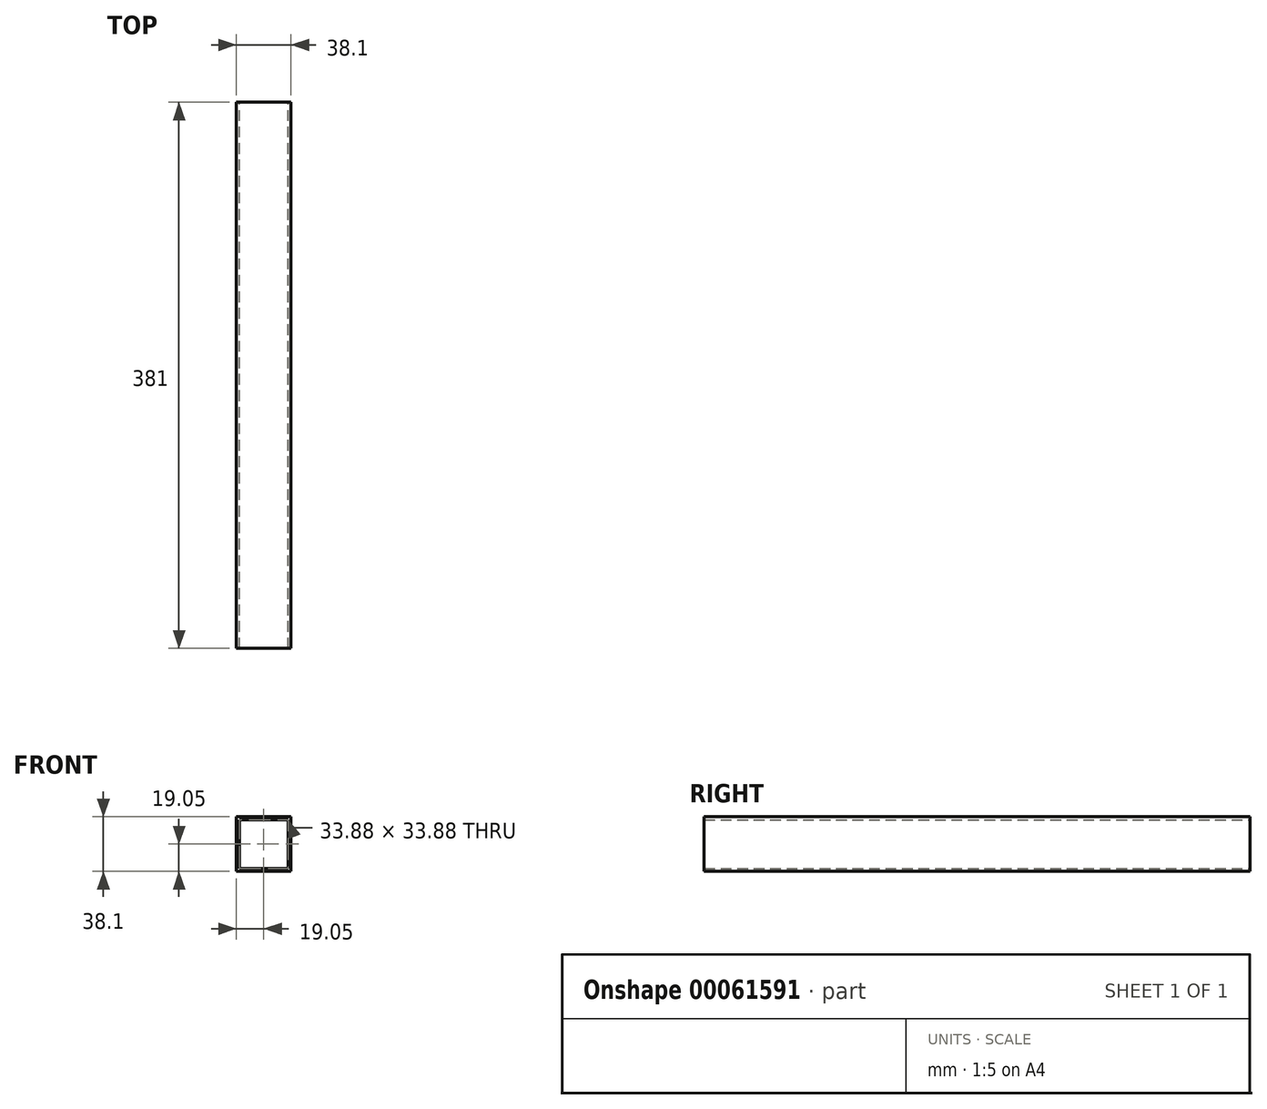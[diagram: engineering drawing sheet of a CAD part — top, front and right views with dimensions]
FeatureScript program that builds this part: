
annotation { "Feature Type Name" : "Feature", "Feature Type Description" : "" }
export const myFeature = defineFeature(function(context is Context, id is Id, definition is map)
    precondition{}
    {
        {
            var Q0;
            Q0=qCreatedBy(makeId("Front.planeOp"),FACE);
            var sketch = newSketch(context, id + "F0", { "sketchPlane" : qUnion([Q0])});
            skLineSegment(sketch, "E0.bottom", {"start": v(-19.05, 19.05) * mm, "end": v(19.05, 19.05) * mm});
            skLineSegment(sketch, "E0.top", {"start": v(-19.05, -19.05) * mm, "end": v(19.05, -19.05) * mm});
            skLineSegment(sketch, "E0.left", {"start": v(-19.05, 19.05) * mm, "end": v(-19.05, -19.05) * mm});
            skLineSegment(sketch, "E0.right", {"start": v(19.05, 19.05) * mm, "end": v(19.05, -19.05) * mm});
            skLineSegment(sketch, "E1.bottom", {"start": v(-16.94, 16.94) * mm, "end": v(16.94, 16.94) * mm});
            skLineSegment(sketch, "E1.top", {"start": v(-16.94, -16.94) * mm, "end": v(16.94, -16.94) * mm});
            skLineSegment(sketch, "E1.left", {"start": v(-16.94, 16.94) * mm, "end": v(-16.94, -16.94) * mm});
            skLineSegment(sketch, "E1.right", {"start": v(16.94, 16.94) * mm, "end": v(16.94, -16.94) * mm});
            skLineSegment(sketch, "E2", {"start": v(-19.05, 19.05) * mm, "end": v(19.05, -19.05) * mm, "construction": true});
            skSolve(sketch);
        }
        {
            var Q0;
            Q0=makeQuery(id+"F0.imprint","IMPRINT",FACE,{"disambiguationData":[TD([[makeQuery(id+"F0.imprint","IMPRINT",EDGE,{"derivedFrom":sQuery(id+"F0.wireOp",EDGE,"E0.bottom")}),-1.0]])]});
            extrude(context, id + "F1", {"entities" : qUnion([Q0]), "endBound" : BoundingType.SYMMETRIC, "depth" : 381 * mm});
        }
    });
